# Revit family: PRD_FrankeWS_SpprtRls_GrabRail_CNTX50WL,WR
name_source: partatom
category: Furniture
revit_build: Autodesk Revit 2018 (Build: 20190510_1515(x64)
units: mm (PartAtom-declared; Revit-internal decimal feet)

## family parameters
Cut with Voids When Loaded = No
Host = Face
OmniClass Number = 23.40.20.21
OmniClass Title = Toilet and Bath Specialties
Room Calculation Point = No
Shared = No

## types (2) — shared parameters
AssetType = Fixed
Category = Pr_40_20_76_84, Support rails
Color = no colour
Default Elevation = 750 mm  [stored 2.46063 ft]
Description = 90° angle two way bar for wall mounting, horizontal and vertical, stainless steel, surface satin finished, rough polishing for better surface feel, 32 mm pipe diameter, material thickness 1.2 mm, wall distance 82 mm, with four stainless steel covers for hidden mounting, incl. stainless steel screws and dowels.
DurationUnit = year
Features = stainless steel, surface satin finished
Finish = satin finished
GrabRailMaterial = PRD_AR_StainlessSteel_SatinFinished
GrossWeight = 2.99 kg
HiddenFixing = YES
Hinged = NO
IfcExportAs = IfcFurnitureType
IfcExportType = USERDEFINED
MainColor = stainless steel
Manufacturer = KWC Group AG
ManufacturerName = KWC Group AG
ManufacturerURL = www.kwc.com
Material = stainless steel
MaterialCode = 1.4301
MaterialFinish = Satin finished
MaterialThickness = 1.20 mm
MaterialsBody = Stainless steel 1.4301
NBSDescription = Support rails
NBSReference = 45-35-72/360
NetWeight = 2.67 kg
NominalDepth = 726 mm  [stored 2.38189 ft]
NominalHeight = 983 mm  [stored 3.22507 ft]
NominalWidth = 806 mm  [stored 2.64436 ft]
NumberOfFixingPoints = 4
PipeDiameter = 32  [stored 0.104987 ft]
ProductInformation = https://pim.kwc.com
Size = 806 x 983 x 726 mm
TypeOfFixing = SCREW
TypeOfGrabRail = ANGLE-BAR
TypeOfMounting = WALL-MOUNTING
URL = www.kwc.com
Uniclass2015Code = Pr_40_20_76_84
Uniclass2015Title = Support rails
Uniclass2015Version = Products v1.10
Version = 1
WarrantyDurationUnit = year

## per-type parameters (varying)
| type | BIMObjectName | CNTX50WL | CNTX50WR | Direction | ModelNumber | Name |
| CNTX50WL | PRD_AR_SpprtRls_GrabRail_CNTX50WL | Yes | No | Left | 2030038227 | Grab Rail CNTX50WL |
| CNTX50WR | PRD_AR_SpprtRls_GrabRail_CNTX50WR | No | Yes | Right | 2030038228 | Grab Rail CNTX50WR |

note: column(s) folded — value = type name in every type: Model, ModelReference

note: [stored X ft] marks values corroborated as IEEE doubles in the binary element streams (Revit-internal decimal feet)

## geometry (parser evidence)
native form markers: Sweep x2
no freeform markers — native parametric forms only
